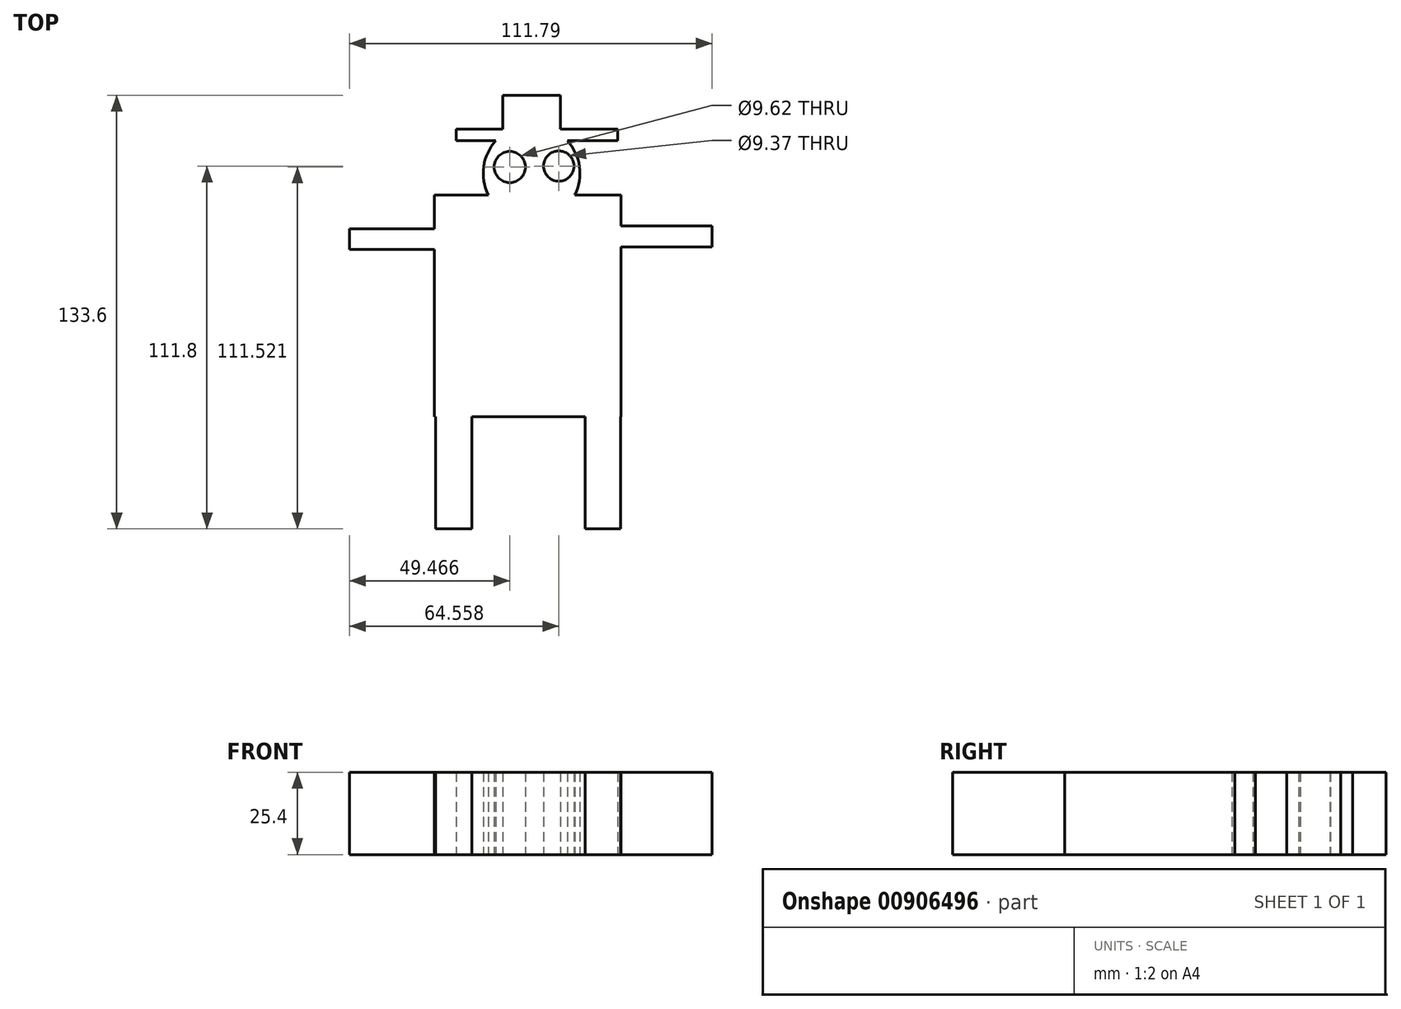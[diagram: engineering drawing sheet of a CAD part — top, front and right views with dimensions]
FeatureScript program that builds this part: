
annotation { "Feature Type Name" : "Feature", "Feature Type Description" : "" }
export const myFeature = defineFeature(function(context is Context, id is Id, definition is map)
    precondition{}
    {
        {
            var Q0;
            Q0=qCreatedBy(makeId("Top.planeOp"),FACE);
            var sketch = newSketch(context, id + "F0", { "sketchPlane" : qUnion([Q0])});
            skLineSegment(sketch, "E0.bottom", {"start": v(-27.01, 29.93) * mm, "end": v(30.51, 29.93) * mm});
            skLineSegment(sketch, "E0.top", {"start": v(-27.01, -38.4) * mm, "end": v(30.51, -38.4) * mm});
            skLineSegment(sketch, "E0.left", {"start": v(-27.01, 29.93) * mm, "end": v(-27.01, -38.4) * mm});
            skLineSegment(sketch, "E0.right", {"start": v(30.51, 29.93) * mm, "end": v(30.51, -38.4) * mm});
            skSolve(sketch);
        }
        {
            var Q0;
            Q0=makeQuery(id+"F0.imprint","IMPRINT",FACE,{"disambiguationData":[TD([[makeQuery(id+"F0.imprint","IMPRINT",EDGE,{"derivedFrom":sQuery(id+"F0.wireOp",EDGE,"E0.bottom")}),-1.0]])]});
            extrude(context, id + "F1", {"entities" : qUnion([Q0]), "depth" : 25.4 * mm, "offsetDistance" : 25.4 * mm});
        }
        {
            var Q0;
            Q0=qCreatedBy(makeId("Top.planeOp"),FACE);
            var sketch = newSketch(context, id + "F2", { "sketchPlane" : qUnion([Q0])});
            skCircle(sketch, "E1", {"center": v(3, 36.58) * mm, "radius": 14.9 * mm});
            skSolve(sketch);
        }
        {
            var Q0;
            Q0=makeQuery(id+"F2.imprint","IMPRINT",FACE,{"disambiguationData":[TD([[makeQuery(id+"F2.imprint","IMPRINT",EDGE,{"derivedFrom":sQuery(id+"F2.wireOp",EDGE,"E1")}),1.0]])]});
            extrude(context, id + "F3", {"entities" : qUnion([Q0]), "operationType" : NewBodyOperationType.ADD, "depth" : 25.4 * mm, "offsetDistance" : 25.4 * mm});
        }
        {
            var Q0;
            Q0=qCreatedBy(makeId("Top.planeOp"),FACE);
            var sketch = newSketch(context, id + "F4", { "sketchPlane" : qUnion([Q0])});
            skLineSegment(sketch, "E2.bottom", {"start": v(29.56, 50.28) * mm, "end": v(-20.2, 50.28) * mm});
            skLineSegment(sketch, "E2.top", {"start": v(29.56, 46.65) * mm, "end": v(-20.2, 46.65) * mm});
            skLineSegment(sketch, "E2.left", {"start": v(29.56, 50.28) * mm, "end": v(29.56, 46.65) * mm});
            skLineSegment(sketch, "E2.right", {"start": v(-20.2, 50.28) * mm, "end": v(-20.2, 46.65) * mm});
            skSolve(sketch);
        }
        {
            var Q0;
            Q0=makeQuery(id+"F4.imprint","IMPRINT",FACE,{"disambiguationData":[TD([[makeQuery(id+"F4.imprint","IMPRINT",EDGE,{"derivedFrom":sQuery(id+"F4.wireOp",EDGE,"E2.bottom")}),1.0]])]});
            extrude(context, id + "F5", {"entities" : qUnion([Q0]), "operationType" : NewBodyOperationType.ADD, "depth" : 25.4 * mm, "offsetDistance" : 25.4 * mm});
        }
        {
            var Q0;
            Q0=qCreatedBy(makeId("Top.planeOp"),FACE);
            var sketch = newSketch(context, id + "F6", { "sketchPlane" : qUnion([Q0])});
            skLineSegment(sketch, "E3.bottom", {"start": v(11.95, 47.2) * mm, "end": v(-5.94, 47.2) * mm});
            skLineSegment(sketch, "E3.top", {"start": v(11.95, 60.62) * mm, "end": v(-5.94, 60.62) * mm});
            skLineSegment(sketch, "E3.left", {"start": v(11.95, 47.2) * mm, "end": v(11.95, 60.62) * mm});
            skLineSegment(sketch, "E3.right", {"start": v(-5.94, 47.2) * mm, "end": v(-5.94, 60.62) * mm});
            skSolve(sketch);
        }
        {
            var Q0;
            Q0=makeQuery(id+"F6.imprint","IMPRINT",FACE,{"disambiguationData":[TD([[makeQuery(id+"F6.imprint","IMPRINT",EDGE,{"derivedFrom":sQuery(id+"F6.wireOp",EDGE,"E3.bottom")}),-1.0]])]});
            extrude(context, id + "F7", {"entities" : qUnion([Q0]), "operationType" : NewBodyOperationType.ADD, "depth" : 25.4 * mm, "offsetDistance" : 25.4 * mm});
        }
        {
            var Q0;
            Q0=qCreatedBy(makeId("Top.planeOp"),FACE);
            var sketch = newSketch(context, id + "F8", { "sketchPlane" : qUnion([Q0])});
            skLineSegment(sketch, "E4.bottom", {"start": v(27.04, 20.37) * mm, "end": v(58.62, 20.37) * mm});
            skLineSegment(sketch, "E4.top", {"start": v(27.04, 13.95) * mm, "end": v(58.62, 13.95) * mm});
            skLineSegment(sketch, "E4.left", {"start": v(27.04, 20.37) * mm, "end": v(27.04, 13.95) * mm});
            skLineSegment(sketch, "E4.right", {"start": v(58.62, 20.37) * mm, "end": v(58.62, 13.95) * mm});
            skLineSegment(sketch, "E5.bottom", {"start": v(-22.15, 19.54) * mm, "end": v(-53.17, 19.54) * mm});
            skLineSegment(sketch, "E5.top", {"start": v(-22.15, 13.1) * mm, "end": v(-53.17, 13.1) * mm});
            skLineSegment(sketch, "E5.left", {"start": v(-22.15, 19.54) * mm, "end": v(-22.15, 13.1) * mm});
            skLineSegment(sketch, "E5.right", {"start": v(-53.17, 19.54) * mm, "end": v(-53.17, 13.1) * mm});
            skSolve(sketch);
        }
        {
            var Q0;
            Q0=makeQuery(id+"F8.imprint","IMPRINT",FACE,{"disambiguationData":[TD([[makeQuery(id+"F8.imprint","IMPRINT",EDGE,{"derivedFrom":sQuery(id+"F8.wireOp",EDGE,"E4.bottom")}),-1.0]])]});
            var Q1;
            Q1=makeQuery(id+"F8.imprint","IMPRINT",FACE,{"disambiguationData":[TD([[makeQuery(id+"F8.imprint","IMPRINT",EDGE,{"derivedFrom":sQuery(id+"F8.wireOp",EDGE,"E5.bottom")}),1.0]])]});
            extrude(context, id + "F9", {"entities" : qUnion([Q0, Q1]), "operationType" : NewBodyOperationType.ADD, "depth" : 25.4 * mm, "offsetDistance" : 25.4 * mm});
        }
        {
            var Q0;
            Q0=qCreatedBy(makeId("Top.planeOp"),FACE);
            var sketch = newSketch(context, id + "F10", { "sketchPlane" : qUnion([Q0])});
            skLineSegment(sketch, "E6.bottom", {"start": v(30.4, -38.04) * mm, "end": v(19.5, -38.04) * mm});
            skLineSegment(sketch, "E6.top", {"start": v(30.4, -72.98) * mm, "end": v(19.5, -72.98) * mm});
            skLineSegment(sketch, "E6.left", {"start": v(30.4, -38.04) * mm, "end": v(30.4, -72.98) * mm});
            skLineSegment(sketch, "E6.right", {"start": v(19.5, -38.04) * mm, "end": v(19.5, -72.98) * mm});
            skLineSegment(sketch, "E7.bottom", {"start": v(-26.62, -37.76) * mm, "end": v(-15.44, -37.76) * mm});
            skLineSegment(sketch, "E7.top", {"start": v(-26.62, -72.98) * mm, "end": v(-15.44, -72.98) * mm});
            skLineSegment(sketch, "E7.left", {"start": v(-26.62, -37.76) * mm, "end": v(-26.62, -72.98) * mm});
            skLineSegment(sketch, "E7.right", {"start": v(-15.44, -37.76) * mm, "end": v(-15.44, -72.98) * mm});
            skSolve(sketch);
        }
        {
            var Q0;
            Q0=makeQuery(id+"F10.imprint","IMPRINT",FACE,{"disambiguationData":[TD([[makeQuery(id+"F10.imprint","IMPRINT",EDGE,{"derivedFrom":sQuery(id+"F10.wireOp",EDGE,"E6.bottom")}),1.0]])]});
            var Q1;
            Q1=makeQuery(id+"F10.imprint","IMPRINT",FACE,{"disambiguationData":[TD([[makeQuery(id+"F10.imprint","IMPRINT",EDGE,{"derivedFrom":sQuery(id+"F10.wireOp",EDGE,"E7.bottom")}),-1.0]])]});
            extrude(context, id + "F11", {"entities" : qUnion([Q0, Q1]), "operationType" : NewBodyOperationType.ADD, "depth" : 25.4 * mm, "offsetDistance" : 25.4 * mm});
        }
        {
            var Q0;
            Q0=qCreatedBy(makeId("Top.planeOp"),FACE);
            var sketch = newSketch(context, id + "F12", { "sketchPlane" : qUnion([Q0])});
            skCircle(sketch, "E8", {"center": v(11.39, 38.82) * mm, "radius": 4.69 * mm});
            skCircle(sketch, "E9", {"center": v(-3.7, 38.54) * mm, "radius": 4.8 * mm});
            skSolve(sketch);
        }
        {
            var Q0;
            Q0=makeQuery(id+"F12.imprint","IMPRINT",FACE,{"disambiguationData":[TD([[makeQuery(id+"F12.imprint","IMPRINT",EDGE,{"derivedFrom":sQuery(id+"F12.wireOp",EDGE,"E8")}),1.0]])]});
            var Q1;
            Q1=makeQuery(id+"F12.imprint","IMPRINT",FACE,{"disambiguationData":[TD([[makeQuery(id+"F12.imprint","IMPRINT",EDGE,{"derivedFrom":sQuery(id+"F12.wireOp",EDGE,"E9")}),1.0]])]});
            extrude(context, id + "F13", {"entities" : qUnion([Q0, Q1]), "operationType" : NewBodyOperationType.REMOVE, "depth" : 25.4 * mm, "offsetDistance" : 25.4 * mm});
        }
    });
